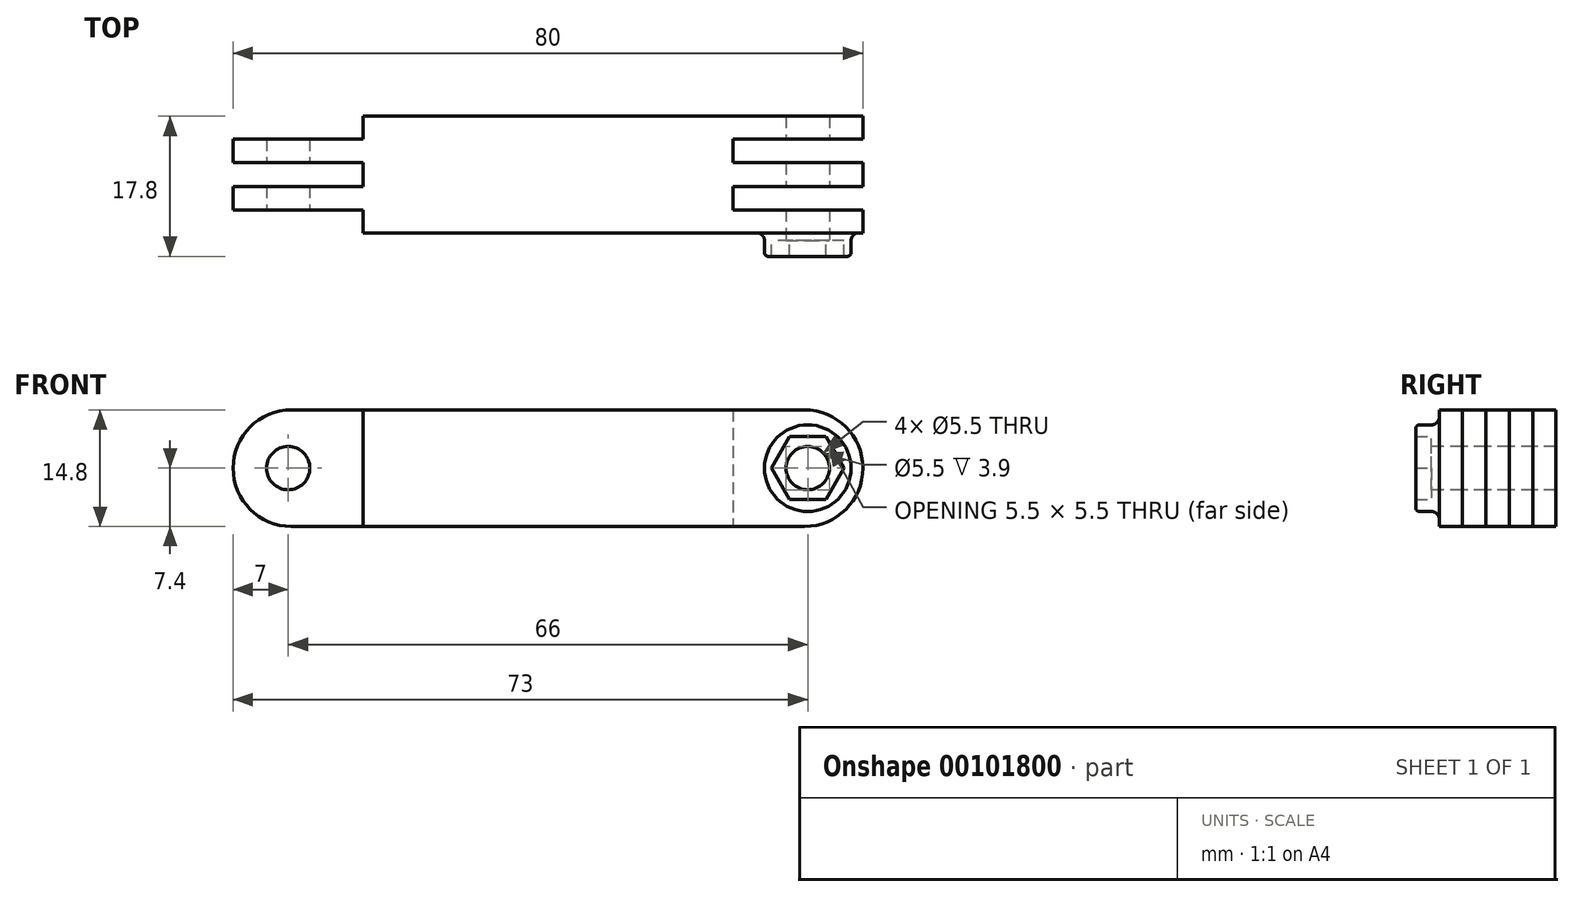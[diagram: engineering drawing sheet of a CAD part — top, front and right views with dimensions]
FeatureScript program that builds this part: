
annotation { "Feature Type Name" : "Feature", "Feature Type Description" : "" }
export const myFeature = defineFeature(function(context is Context, id is Id, definition is map)
    precondition{}
    {
        {
            var Q0;
            Q0=qCreatedBy(makeId("Front.planeOp"),FACE);
            var sketch = newSketch(context, id + "F0", { "sketchPlane" : qUnion([Q0])});
            skLineSegment(sketch, "E0.bottom", {"start": v(32.6, -7.4) * mm, "end": v(-32.6, -7.4) * mm});
            skLineSegment(sketch, "E0.top", {"start": v(32.6, 7.4) * mm, "end": v(-32.6, 7.4) * mm});
            skLineSegment(sketch, "E0.left", {"start": v(40, 0) * mm, "end": v(40, 0) * mm});
            skLineSegment(sketch, "E0.right", {"start": v(-40, 0) * mm, "end": v(-40, 0) * mm});
            skPoint(sketch, "E0.middle", {"position": v(0, 0) * mm});
            skPoint(sketch, "E1.visualSharp", {"position": v(-40, 7.4) * mm});
            skArc(sketch, "E1.filletArc", {"start": v(-32.6, 7.4) * mm, "mid": v(-37.83, 5.23) * mm, "end": v(-40, 0) * mm});
            skPoint(sketch, "E2.visualSharp", {"position": v(40, 7.4) * mm});
            skArc(sketch, "E2.filletArc", {"start": v(40, 0) * mm, "mid": v(37.83, 5.23) * mm, "end": v(32.6, 7.4) * mm});
            skPoint(sketch, "E3.visualSharp", {"position": v(40, -7.4) * mm});
            skArc(sketch, "E3.filletArc", {"start": v(32.6, -7.4) * mm, "mid": v(37.83, -5.23) * mm, "end": v(40, 0) * mm});
            skPoint(sketch, "E4.visualSharp", {"position": v(-40, -7.4) * mm});
            skArc(sketch, "E4.filletArc", {"start": v(-40, 0) * mm, "mid": v(-37.83, -5.23) * mm, "end": v(-32.6, -7.4) * mm});
            skSolve(sketch);
        }
        {
            var Q0;
            Q0=makeQuery(id+"F0.imprint","IMPRINT",FACE,{"disambiguationData":[TD([[makeQuery(id+"F0.imprint","IMPRINT",EDGE,{"derivedFrom":sQuery(id+"F0.wireOp",EDGE,"E0.bottom")}),-1.0]])]});
            extrude(context, id + "F1", {"entities" : qUnion([Q0]), "flatOperationType" : FlatOperationType.REMOVE, "offsetDistance" : 25 * mm, "depth" : 7.4 * mm, "hasSecondDirection" : true, "secondDirectionOppositeDirection" : true, "secondDirectionDepth" : 7.4 * mm, "domain" : OperationDomain.MODEL});
        }
        {
            var Q0;
            Q0=qCreatedBy(makeId("Front.planeOp"),FACE);
            var sketch = newSketch(context, id + "F2", { "sketchPlane" : qUnion([Q0])});
            skCircle(sketch, "E5", {"center": v(-33, 0) * mm, "radius": 2.75 * mm});
            skCircle(sketch, "E6", {"center": v(33, 0) * mm, "radius": 2.75 * mm});
            skSolve(sketch);
        }
        {
            var Q0;
            Q0=qCreatedBy(makeId("Top.planeOp"),FACE);
            var sketch = newSketch(context, id + "F3", { "sketchPlane" : qUnion([Q0])});
            skLineSegment(sketch, "E7.bottom", {"start": v(-41.5, 7.5) * mm, "end": v(-23.5, 7.5) * mm});
            skLineSegment(sketch, "E7.top", {"start": v(-41.5, 4.5) * mm, "end": v(-23.5, 4.5) * mm});
            skLineSegment(sketch, "E7.left", {"start": v(-41.5, 7.5) * mm, "end": v(-41.5, 4.5) * mm});
            skLineSegment(sketch, "E7.right", {"start": v(-23.5, 7.5) * mm, "end": v(-23.5, 4.5) * mm});
            skLineSegment(sketch, "E8.0.1.0", {"start": v(-41.5, 1.5) * mm, "end": v(-41.5, -1.5) * mm});
            skLineSegment(sketch, "E8.0.1.1", {"start": v(-41.5, 1.5) * mm, "end": v(-23.5, 1.5) * mm});
            skLineSegment(sketch, "E8.0.1.2", {"start": v(-23.5, 1.5) * mm, "end": v(-23.5, -1.5) * mm});
            skLineSegment(sketch, "E8.0.1.3", {"start": v(-41.5, -1.5) * mm, "end": v(-23.5, -1.5) * mm});
            skLineSegment(sketch, "E8.0.2.0", {"start": v(-41.5, -4.5) * mm, "end": v(-41.5, -7.5) * mm});
            skLineSegment(sketch, "E8.0.2.1", {"start": v(-41.5, -4.5) * mm, "end": v(-23.5, -4.5) * mm});
            skLineSegment(sketch, "E8.0.2.2", {"start": v(-23.5, -4.5) * mm, "end": v(-23.5, -7.5) * mm});
            skLineSegment(sketch, "E8.0.2.3", {"start": v(-41.5, -7.5) * mm, "end": v(-23.5, -7.5) * mm});
            skLineSegment(sketch, "E8.direction1", {"start": v(-41.5, 4.5) * mm, "end": v(-16.5, 4.5) * mm, "construction": true});
            skLineSegment(sketch, "E8.direction2", {"start": v(-41.5, 4.5) * mm, "end": v(-41.5, -1.5) * mm, "construction": true});
            skLineSegment(sketch, "E9.bottom", {"start": v(23.5, 4.5) * mm, "end": v(41.5, 4.5) * mm});
            skLineSegment(sketch, "E9.top", {"start": v(23.5, 1.5) * mm, "end": v(41.5, 1.5) * mm});
            skLineSegment(sketch, "E9.left", {"start": v(23.5, 4.5) * mm, "end": v(23.5, 1.5) * mm});
            skLineSegment(sketch, "E9.right", {"start": v(41.5, 4.5) * mm, "end": v(41.5, 1.5) * mm});
            skLineSegment(sketch, "E10.0.1.0", {"start": v(23.5, -1.5) * mm, "end": v(41.5, -1.5) * mm});
            skLineSegment(sketch, "E10.0.1.1", {"start": v(23.5, -1.5) * mm, "end": v(23.5, -4.5) * mm});
            skLineSegment(sketch, "E10.0.1.2", {"start": v(23.5, -4.5) * mm, "end": v(41.5, -4.5) * mm});
            skLineSegment(sketch, "E10.0.1.3", {"start": v(41.5, -1.5) * mm, "end": v(41.5, -4.5) * mm});
            skLineSegment(sketch, "E10.direction1", {"start": v(23.5, 4.5) * mm, "end": v(48.5, 4.5) * mm, "construction": true});
            skLineSegment(sketch, "E10.direction2", {"start": v(23.5, 4.5) * mm, "end": v(23.5, -1.5) * mm, "construction": true});
            skSolve(sketch);
        }
        {
            var Q0;
            Q0 = qSketchRegion(id + "F3", true);
            extrude(context, id + "F4", {"entities" : qUnion([Q0]), "operationType" : NewBodyOperationType.REMOVE, "depth" : 25 * mm, "hasSecondDirection" : true, "secondDirectionOppositeDirection" : true, "secondDirectionDepth" : 25 * mm});
        }
        {
            var Q0;
            Q0 = qSketchRegion(id + "F2", true);
            extrude(context, id + "F5", {"entities" : qUnion([Q0]), "operationType" : NewBodyOperationType.REMOVE, "oppositeDirection" : true, "depth" : 25 * mm, "hasSecondDirection" : true, "secondDirectionOppositeDirection" : false, "secondDirectionDepth" : 25 * mm});
        }
        {
            var Q0;
            Q0=makeQuery(id+"F1.opExtrude","CAP_FACE",FACE,{"disambiguationData":[OSD([sQuery(id+"F0.wireOp",EDGE,"E0.bottom"),sQuery(id+"F0.wireOp",EDGE,"E0.top"),sQuery(id+"F0.wireOp",EDGE,"E1.filletArc"),sQuery(id+"F0.wireOp",EDGE,"E2.filletArc"),sQuery(id+"F0.wireOp",EDGE,"E3.filletArc"),sQuery(id+"F0.wireOp",EDGE,"E4.filletArc")])],"isStart":false});
            var sketch = newSketch(context, id + "F6", { "sketchPlane" : qUnion([Q0])});
            skCircle(sketch, "E11.cCircle", {"center": v(33, 0) * mm, "radius": 4 * mm, "construction": true});
            skLineSegment(sketch, "E11.0", {"start": v(35.3, -4) * mm, "end": v(30.7, -4) * mm});
            skLineSegment(sketch, "E11.1", {"start": v(30.7, -4) * mm, "end": v(28.38, 0) * mm});
            skLineSegment(sketch, "E11.2", {"start": v(28.38, 0) * mm, "end": v(30.7, 4) * mm});
            skLineSegment(sketch, "E11.3", {"start": v(30.7, 4) * mm, "end": v(35.3, 4) * mm});
            skLineSegment(sketch, "E11.4", {"start": v(35.3, 4) * mm, "end": v(37.62, 0) * mm});
            skLineSegment(sketch, "E11.5", {"start": v(37.62, 0) * mm, "end": v(35.3, -4) * mm});
            skPoint(sketch, "E11.0.midPoint", {"position": v(33, -4) * mm});
            skCircle(sketch, "E12", {"center": v(33, 0) * mm, "radius": 5.5 * mm});
            skSolve(sketch);
        }
        {
            var Q0;
            Q0=makeQuery(id+"F6.imprint","IMPRINT",FACE,{"disambiguationData":[TD([[makeQuery(id+"F6.imprint","IMPRINT",EDGE,{"derivedFrom":sQuery(id+"F6.wireOp",EDGE,"E11.0")}),1.0]])]});
            extrude(context, id + "F7", {"entities" : qUnion([Q0]), "operationType" : NewBodyOperationType.ADD, "depth" : 3 * mm});
        }
        {
            var Q0;
            Q0=makeQuery(id+"F7.opExtrude","CAP_EDGE",EDGE,{"disambiguationData":[OSD([sQuery(id+"F6.wireOp",EDGE,"E12")])],"isStart":false});
            fillet(context, id + "F8", {"entities" : qUnion([Q0]), "radius" : 0.5 * mm, "tangentPropagation" : true, "allowEdgeOverflow" : false});
        }
        {
            var Q0;
            Q0=makeQuery(id+"F7.opExtrude","CAP_EDGE",EDGE,{"disambiguationData":[OSD([sQuery(id+"F6.wireOp",EDGE,"E12")])],"isStart":true});
            fillet(context, id + "F9", {"entities" : qUnion([Q0]), "radius" : 1 * mm, "tangentPropagation" : true, "allowEdgeOverflow" : false});
        }
        {
            var Q0;
            Q0=makeQuery(id+"F7.boolean.opBoolean","SPLIT",FACE,{"disambiguationData":[TD([makeQuery(id+"F5.boolean.opBoolean","COPY",FACE,{"disambiguationData":[OD(2.0)],"derivedFrom":makeQuery(id+"F5.opExtrude","SWEPT_FACE",FACE,{"disambiguationData":[OSD([sQuery(id+"F2.wireOp",EDGE,"E6")])]})})])],"derivedFrom":makeQuery(id+"F1.opExtrude","CAP_FACE",FACE,{"disambiguationData":[OSD([sQuery(id+"F0.wireOp",EDGE,"E0.bottom"),sQuery(id+"F0.wireOp",EDGE,"E0.top"),sQuery(id+"F0.wireOp",EDGE,"E1.filletArc"),sQuery(id+"F0.wireOp",EDGE,"E2.filletArc"),sQuery(id+"F0.wireOp",EDGE,"E3.filletArc"),sQuery(id+"F0.wireOp",EDGE,"E4.filletArc")])],"isStart":false})});
            extrude(context, id + "F10", {"entities" : qUnion([Q0]), "operationType" : NewBodyOperationType.ADD, "depth" : 1 * mm});
        }
    });
